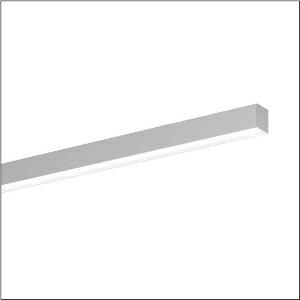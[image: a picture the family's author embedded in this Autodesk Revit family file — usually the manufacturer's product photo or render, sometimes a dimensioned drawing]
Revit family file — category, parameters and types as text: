
# Revit family: silica_r__21_51mx20dc45sb_4e07
name_source: partatom
category: Lighting Fixtures
units: mm (PartAtom-declared; Revit-internal decimal feet)

## family parameters
Cut with Voids When Loaded = No
Host = Face
Light Source = No
Part Type = Normal
Room Calculation Point = No
Round Connector Dimension = Use Diameter
Shared = No

## types (1)
- --- (1 x LED, 6000 lm, 40.1 W, 4000K)
    Apparent Load = 40 VA
    CIE Flux Codes = 48 79 96 100 100
    Color Rendering = 80
    Color Temperature = 4000K
    Default Elevation = 1800 mm
    Description = Silica® 21, office luminaire, primary optical cover: cover, of PMMA, opal, light emission: direct distribution, primary light characteristic: symmetric, installation type: surface-mounted, LED, rated luminous flux: 6.000lm, luminous efficacy: 150lm/W, light colour: 840, colour temperature: 4000K, with terminal, 3+2-pole, max. 2.5mm², mains connection: 220..240V, AC, 50/60Hz, rated input power: 40.1W, luminaire housing, of aluminium, metallic grey (RAL 9006), length: 3.004mm, width: 53mm, height: 53mm, protection rating (complete): IP20, insulation class (complete): insulation class I (protective earthing), certification: CE, permissible operating ambient temperature: 0..+35°C, standard: EN 50419, packaging unit: 1 piece
    Height = 0 mm  [stored 0 ft]
    Lamp = 1 x LED
    Lamp Light Flux = 6000 lm
    Lamp Power = 40.1 W
    Lamp count = 1
    Length = 3004 mm
    Luminous efficacy = 150 lm/W
    Manufacturer = Siteco
    ModVariant = No
    Model = 51MX20DC45SB
    Mounting Place = Ceiling
    Mounting Type = Recessed
    Number of Poles = 1
    OnlyDefault = Yes
    Power Factor = 1
    Product Name = Silica® 21
    Product group = office luminaire | ceiling recessed
    ProductGroupID = 401
    Protection Class = Protection class I
    Protection Degree = IP 20
    RLX_Detail_Level = 1
    RLX_Emergency_Light_Flux = 0 lm
    RLX_Emergency_Type = 0
    RLX_Emergency_Type_DB = No
    RlxData = <blob elided: 26425 chars, md5=c1098984>
    Socket = socket
    Standby Power = 0 W
    System Light Flux = 6000 lm
    System Power = 40 W
    Type Comments = factory setting: luminous flux: 100 % | dim-lin: 254 | 218 mA
    Type Image = l_1297768.jpg
    URL = http://relux.com
    VarID = @adj_047879
    Voltage = 0 V
    Weight = 0.00 kg
    Width = 53 mm

note: [stored X ft] marks values corroborated as IEEE doubles in the binary element streams (Revit-internal decimal feet)

## geometry (parser evidence)
native form markers: Blend x4, Sweep x9
no freeform markers — native parametric forms only
